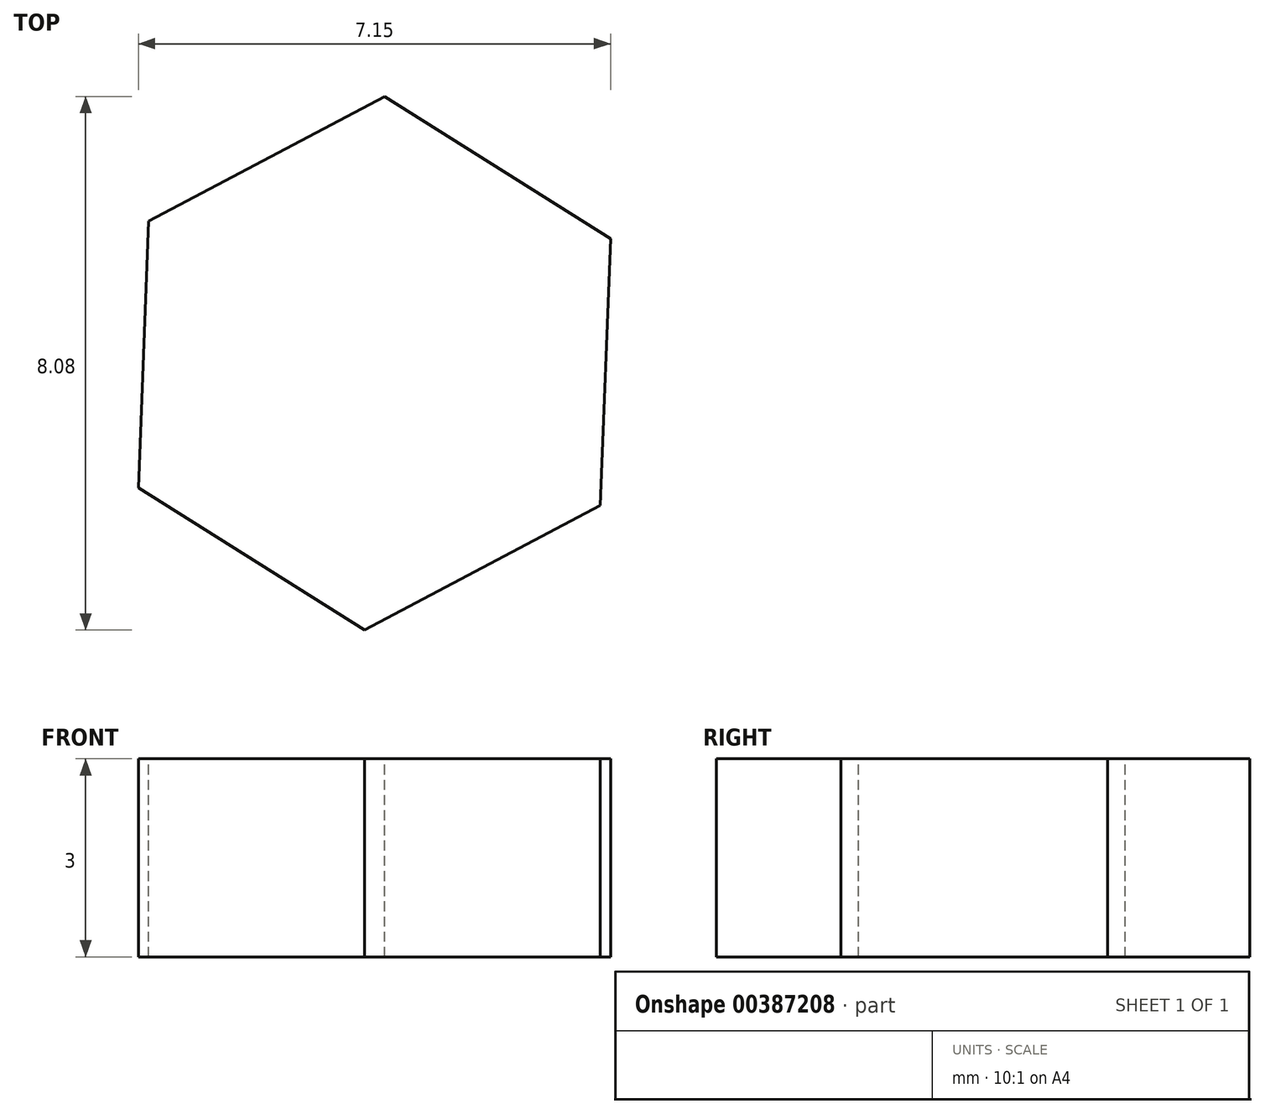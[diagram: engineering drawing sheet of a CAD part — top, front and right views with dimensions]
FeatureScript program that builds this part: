
annotation { "Feature Type Name" : "Feature", "Feature Type Description" : "" }
export const myFeature = defineFeature(function(context is Context, id is Id, definition is map)
    precondition{}
    {
        {
            var Q0;
            Q0=qCreatedBy(makeId("Top.planeOp"),FACE);
            var sketch = newSketch(context, id + "F0", { "sketchPlane" : qUnion([Q0])});
            skCircle(sketch, "E0.cCircle", {"center": v(-3.57, 0) * mm, "radius": 4.04 * mm, "construction": true});
            skLineSegment(sketch, "E0.0", {"start": v(0, 1.89) * mm, "end": v(-0.15, -2.15) * mm});
            skLineSegment(sketch, "E0.1", {"start": v(-0.15, -2.15) * mm, "end": v(-3.73, -4.04) * mm});
            skLineSegment(sketch, "E0.2", {"start": v(-3.73, -4.04) * mm, "end": v(-7.15, -1.89) * mm});
            skLineSegment(sketch, "E0.3", {"start": v(-7.15, -1.89) * mm, "end": v(-7, 2.15) * mm});
            skLineSegment(sketch, "E0.4", {"start": v(-7, 2.15) * mm, "end": v(-3.42, 4.04) * mm});
            skLineSegment(sketch, "E0.5", {"start": v(-3.42, 4.04) * mm, "end": v(0, 1.89) * mm});
            skSolve(sketch);
        }
        {
            var Q0;
            Q0=qSketchRegion(id+"F0",true);
            extrude(context, id + "F1", {"entities" : qUnion([Q0]), "oppositeDirection" : true, "depth" : 3 * mm});
        }
    });
